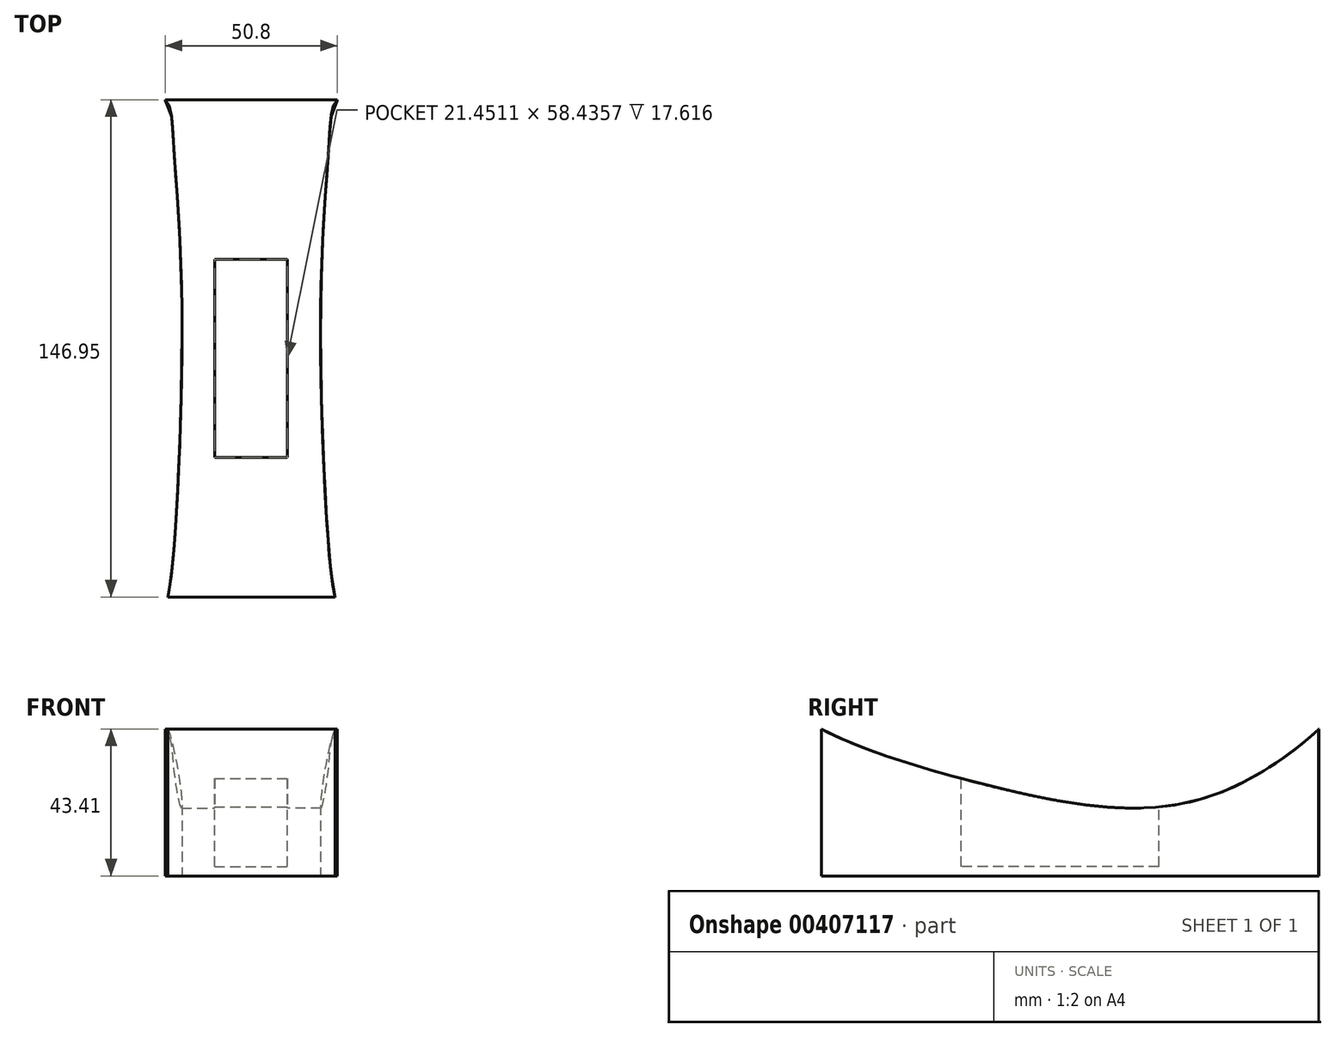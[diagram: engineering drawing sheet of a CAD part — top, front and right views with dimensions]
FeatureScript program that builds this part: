
annotation { "Feature Type Name" : "Feature", "Feature Type Description" : "" }
export const myFeature = defineFeature(function(context is Context, id is Id, definition is map)
    precondition{}
    {
        {
            var Q0;
            Q0=qCreatedBy(makeId("Right.planeOp"),FACE);
            var sketch = newSketch(context, id + "F0", { "sketchPlane" : qUnion([Q0])});
            skLineSegment(sketch, "E0.bottom", {"start": v(-73.72, 21.82) * mm, "end": v(73.23, 21.82) * mm});
            skLineSegment(sketch, "E0.top", {"start": v(-73.72, -21.82) * mm, "end": v(73.23, -21.82) * mm});
            skLineSegment(sketch, "E0.left", {"start": v(-73.72, 21.82) * mm, "end": v(-73.72, -21.82) * mm});
            skLineSegment(sketch, "E0.right", {"start": v(73.23, 21.82) * mm, "end": v(73.23, -21.82) * mm});
            skSolve(sketch);
        }
        {
            var Q0;
            Q0 = qSketchRegion(id + "F0", true);
            extrude(context, id + "F1", {"entities" : qUnion([Q0]), "depth" : 25.4 * mm, "hasSecondDirection" : true, "secondDirectionOppositeDirection" : true, "secondDirectionDepth" : 25.4 * mm});
        }
        {
            var Q0;
            Q0=qCreatedBy(makeId("Right.planeOp"),FACE);
            var sketch = newSketch(context, id + "F2", { "sketchPlane" : qUnion([Q0])});
            skFitSpline(sketch, "E1", {"points": [v(-74.22, 21.82) * mm, v(-22.93, 4.56) * mm, v(35.01, 0) * mm, v(73.48, 21.82) * mm, v(82.6, 36.86) * mm, v(72, 46.97) * mm, v(29.1, 48.94) * mm, v(-32.8, 48.45) * mm, v(-78.16, 47.96) * mm, v(-86.54, 34.64) * mm, v(-74.22, 21.82) * mm]});
            skSolve(sketch);
        }
        {
            var Q0;
            Q0 = qSketchRegion(id + "F2", true);
            extrude(context, id + "F3", {"entities" : qUnion([Q0]), "operationType" : NewBodyOperationType.REMOVE, "oppositeDirection" : true, "depth" : 25.4 * mm, "hasSecondDirection" : true, "secondDirectionOppositeDirection" : false, "secondDirectionDepth" : 25.4 * mm});
        }
        {
            var Q0;
            Q0=qCreatedBy(makeId("Top.planeOp"),FACE);
            var sketch = newSketch(context, id + "F4", { "sketchPlane" : qUnion([Q0])});
            skFitSpline(sketch, "E2", {"points": [v(-25.4, 73.1) * mm, v(-22.93, 60.04) * mm, v(-20.46, 7.03) * mm, v(-24.66, -73.6) * mm, v(-26.88, -75.57) * mm, v(-50.3, -72.12) * mm, v(-61.4, -22.56) * mm, v(-54.5, 45.74) * mm, v(-44.63, 67.19) * mm, v(-39.94, 72.37) * mm, v(-30.82, 72.86) * mm, v(-25.4, 73.1) * mm]});
            skFitSpline(sketch, "E3.MirrorC", {"points": [v(25.4, 73.1) * mm, v(22.93, 60.04) * mm, v(20.46, 7.03) * mm, v(24.66, -73.6) * mm, v(26.88, -75.57) * mm, v(50.3, -72.12) * mm, v(61.4, -22.56) * mm, v(54.5, 45.74) * mm, v(44.63, 67.19) * mm, v(39.94, 72.37) * mm, v(30.82, 72.86) * mm, v(25.4, 73.1) * mm]});
            skSolve(sketch);
        }
        {
            var Q0;
            Q0 = qSketchRegion(id + "F4", true);
            extrude(context, id + "F5", {"entities" : qUnion([Q0]), "operationType" : NewBodyOperationType.REMOVE, "oppositeDirection" : true, "depth" : 25.4 * mm, "hasSecondDirection" : true, "secondDirectionOppositeDirection" : false, "secondDirectionDepth" : 25.4 * mm});
        }
        {
            var Q0;
            Q0=qCreatedBy(makeId("Top.planeOp"),FACE);
            var sketch = newSketch(context, id + "F6", { "sketchPlane" : qUnion([Q0])});
            skLineSegment(sketch, "E4.bottom", {"start": v(-10.85, 26.01) * mm, "end": v(10.6, 26.01) * mm});
            skLineSegment(sketch, "E4.top", {"start": v(-10.85, -32.42) * mm, "end": v(10.6, -32.42) * mm});
            skLineSegment(sketch, "E4.left", {"start": v(-10.85, 26.01) * mm, "end": v(-10.85, -32.42) * mm});
            skLineSegment(sketch, "E4.right", {"start": v(10.6, 26.01) * mm, "end": v(10.6, -32.42) * mm});
            skSolve(sketch);
        }
        {
            var Q0;
            Q0 = qSketchRegion(id + "F6", true);
            extrude(context, id + "F7", {"entities" : qUnion([Q0]), "operationType" : NewBodyOperationType.REMOVE, "oppositeDirection" : true, "depth" : 19.05 * mm, "hasSecondDirection" : true, "secondDirectionOppositeDirection" : false, "secondDirectionDepth" : 19.05 * mm});
        }
    });
